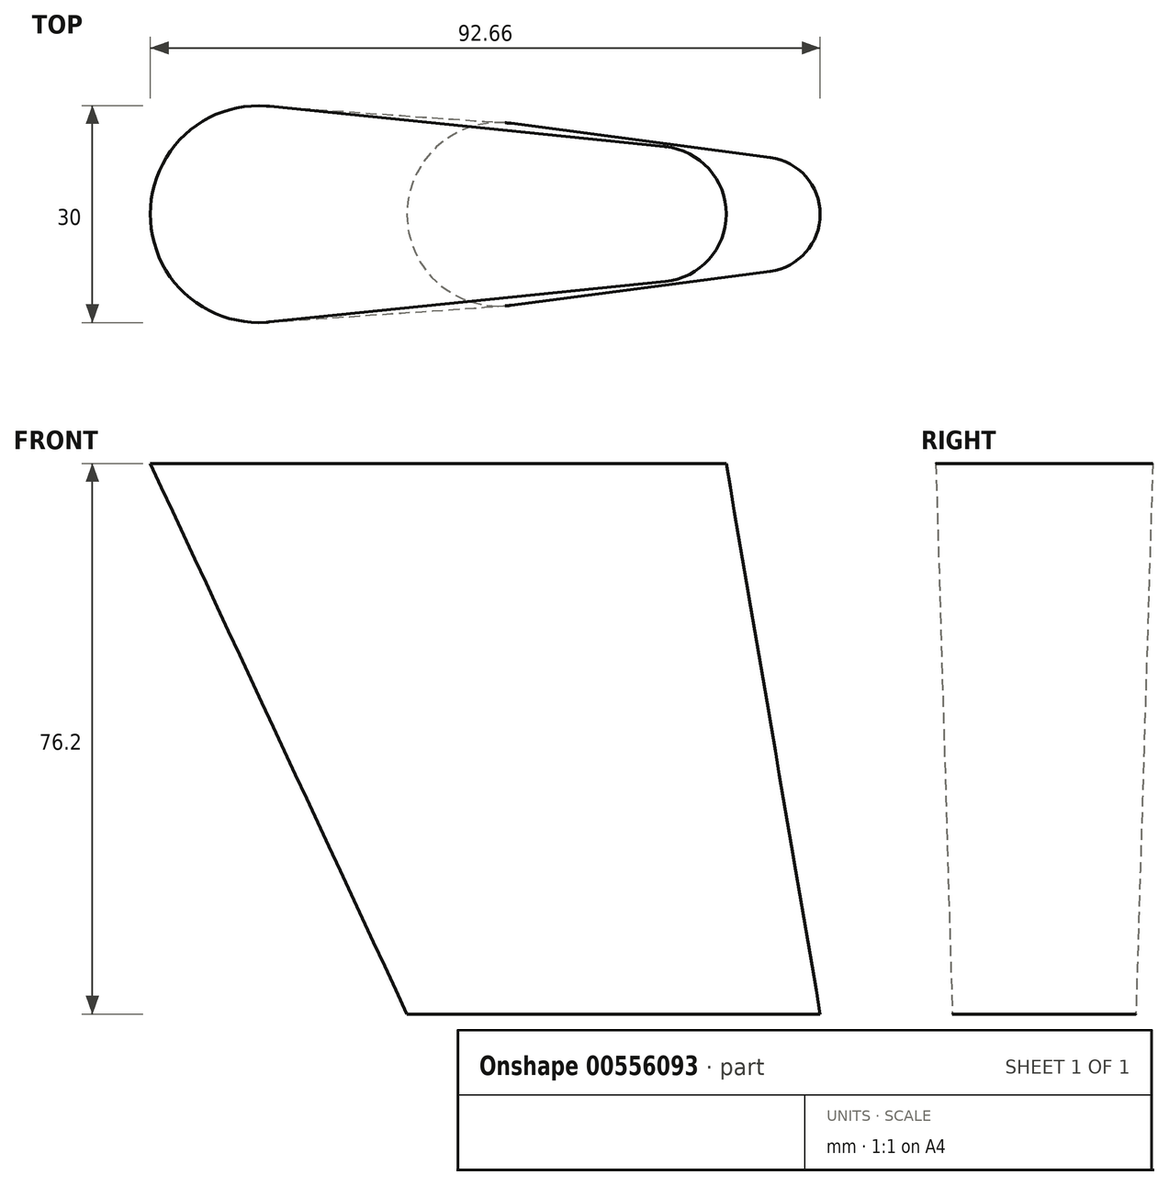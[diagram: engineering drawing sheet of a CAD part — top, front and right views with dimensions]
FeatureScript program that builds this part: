
annotation { "Feature Type Name" : "Feature", "Feature Type Description" : "" }
export const myFeature = defineFeature(function(context is Context, id is Id, definition is map)
    precondition{}
    {
        {
            var Q0;
            Q0=qCreatedBy(makeId("Top.planeOp"),FACE);
            var sketch = newSketch(context, id + "F0", { "sketchPlane" : qUnion([Q0])});
            skArc(sketch, "E0", {"start": v(1.66, 12.6) * mm, "mid": v(-12.7, 0) * mm, "end": v(1.66, -12.6) * mm});
            skArc(sketch, "E1", {"start": v(37.55, -7.87) * mm, "mid": v(44.45, 0) * mm, "end": v(37.55, 7.87) * mm});
            skLineSegment(sketch, "E2", {"start": v(1.66, 12.6) * mm, "end": v(37.55, 7.87) * mm});
            skLineSegment(sketch, "E3", {"start": v(1.66, -12.6) * mm, "end": v(37.55, -7.87) * mm});
            skSolve(sketch);
        }
        {
            var Q0;
            Q0=qCreatedBy(makeId("Top.planeOp"),FACE);
            cPlane(context, id + "F1", {"entities" : qUnion([Q0]), "cplaneType" : CPlaneType.OFFSET, "offset" : 76.2 * mm, "width" : 152.4 * mm, "height" : 152.4 * mm});
        }
        {
            var Q0;
            Q0=qCreatedBy(id+"F1.planeOp",FACE);
            var sketch = newSketch(context, id + "F2", { "sketchPlane" : qUnion([Q0])});
            skArc(sketch, "E4", {"start": v(-31.69, 14.95) * mm, "mid": v(-48.21, 0.03) * mm, "end": v(-31.69, -14.9) * mm});
            skArc(sketch, "E5", {"start": v(23.03, -9.3) * mm, "mid": v(31.45, 0.03) * mm, "end": v(23.03, 9.36) * mm});
            skLineSegment(sketch, "E6", {"start": v(-31.69, 14.95) * mm, "end": v(23.03, 9.36) * mm});
            skLineSegment(sketch, "E7", {"start": v(-31.69, -14.9) * mm, "end": v(23.03, -9.3) * mm});
            skSolve(sketch);
        }
        {
            var Q0;
            Q0=makeQuery(id+"F2.imprint","IMPRINT",FACE,{"disambiguationData":[TD([[makeQuery(id+"F2.imprint","IMPRINT",EDGE,{"derivedFrom":sQuery(id+"F2.wireOp",EDGE,"E4")}),1.0]])]});
            var Q1;
            Q1=makeQuery(id+"F0.imprint","IMPRINT",FACE,{"disambiguationData":[TD([[makeQuery(id+"F0.imprint","IMPRINT",EDGE,{"derivedFrom":sQuery(id+"F0.wireOp",EDGE,"E0")}),1.0]])]});
            loft(context, id + "F3", {"sheetProfilesArray" : [{ "sheetProfileEntities" : qUnion([Q0]) }, { "sheetProfileEntities" : qUnion([Q1]) }]});
        }
    });
